# Revit family: Mailboxes_Vertical-Salsbury_Industries-Surface_Mounted_3500_Series
name_source: partatom
category: Specialty Equipment
revit_build: Autodesk Revit 2016 (Build: 20150714_1515(x64)
units: mm (PartAtom-declared; Revit-internal decimal feet)

## family parameters
Cut with Voids When Loaded = No
Host = Face
OmniClass Number = 23.40.90.14.11
OmniClass Title = Mail Boxes
Part Type = Normal
Room Calculation Point = No
Round Connector Dimension = Use Diameter
Shared = No

## types (5) — shared parameters
Above Finished Floor AFF = 58 "
Assembly Code = C1030910
Assembly Description = Mailboxes
Depth = 7.5 "
Door Location D1 = Vertical Mail Door : Vertical Standard Door
Height = 19 "
Installation Note = 4B+ Vertical Mailboxes are USPS approved for replacement installations.  For new construction, see Cluster Box Units and 4C Horizontal Mailboxes
Lock Material = Stainless Steel - Salsbury Finish -  Polished
Manufacturer = Salsbury Industries
MasterFormat Number = 10 55 00
MasterFormat Title = Postal Specialties
OmniClass 23 Number = 23.40.90.14.11
OmniClass 23 Title = Mail Boxes
Type Comments = Vertical Mailboxes - Surface Mounted
URL = www.mailboxes.com
USPS AFF Param = 58 "
Version = 2.0 (05/31/18)

## per-type parameters (varying)
| type | Description | Door Location D2 | Door Location D3 | Door Location D4 | Door Location D5 | Door Location D6 | Door Location D7 | Width |
| 3507 | 7 Doors - USPS and Private Access | Vertical Mail Door : Vertical Standard Door | Vertical Mail Door : Vertical Standard Door | Vertical Mail Door : Vertical Access Door | Vertical Mail Door : Vertical Standard Door | Vertical Mail Door : Vertical Standard Door | Vertical Mail Door : Vertical Standard Door | 40.75 " |
| 3506 | 6 Doors - USPS and Private Access | Vertical Mail Door : Vertical Standard Door | Vertical Mail Door : Vertical Standard Door | Vertical Mail Door : Vertical Access Door | Vertical Mail Door : Vertical Standard Door | Vertical Mail Door : Vertical Standard Door | Vertical Mail Door : None | 35.25 " |
| 3505 | 5 Doors - USPS and Private Access | Vertical Mail Door : Vertical Standard Door | Vertical Mail Door : Vertical Access Door | Vertical Mail Door : Vertical Standard Door | Vertical Mail Door : Vertical Standard Door | Vertical Mail Door : None | Vertical Mail Door : None | 29.75 " |
| 3504 | 4 Doors - USPS and Private Access | Vertical Mail Door : Vertical Standard Door | Vertical Mail Door : Vertical Access Door | Vertical Mail Door : Vertical Standard Door | Vertical Mail Door : None | Vertical Mail Door : None | Vertical Mail Door : None | 24.25 " |
| 3503 | 3 Doors - USPS and Private Access | Vertical Mail Door : Vertical Access Door | Vertical Mail Door : Vertical Standard Door | Vertical Mail Door : None | Vertical Mail Door : None | Vertical Mail Door : None | Vertical Mail Door : None | 18.75 " |

note: column(s) folded — value = type name in every type: Model

## geometry (parser evidence)
native form markers: Sweep x6
no freeform markers — native parametric forms only
